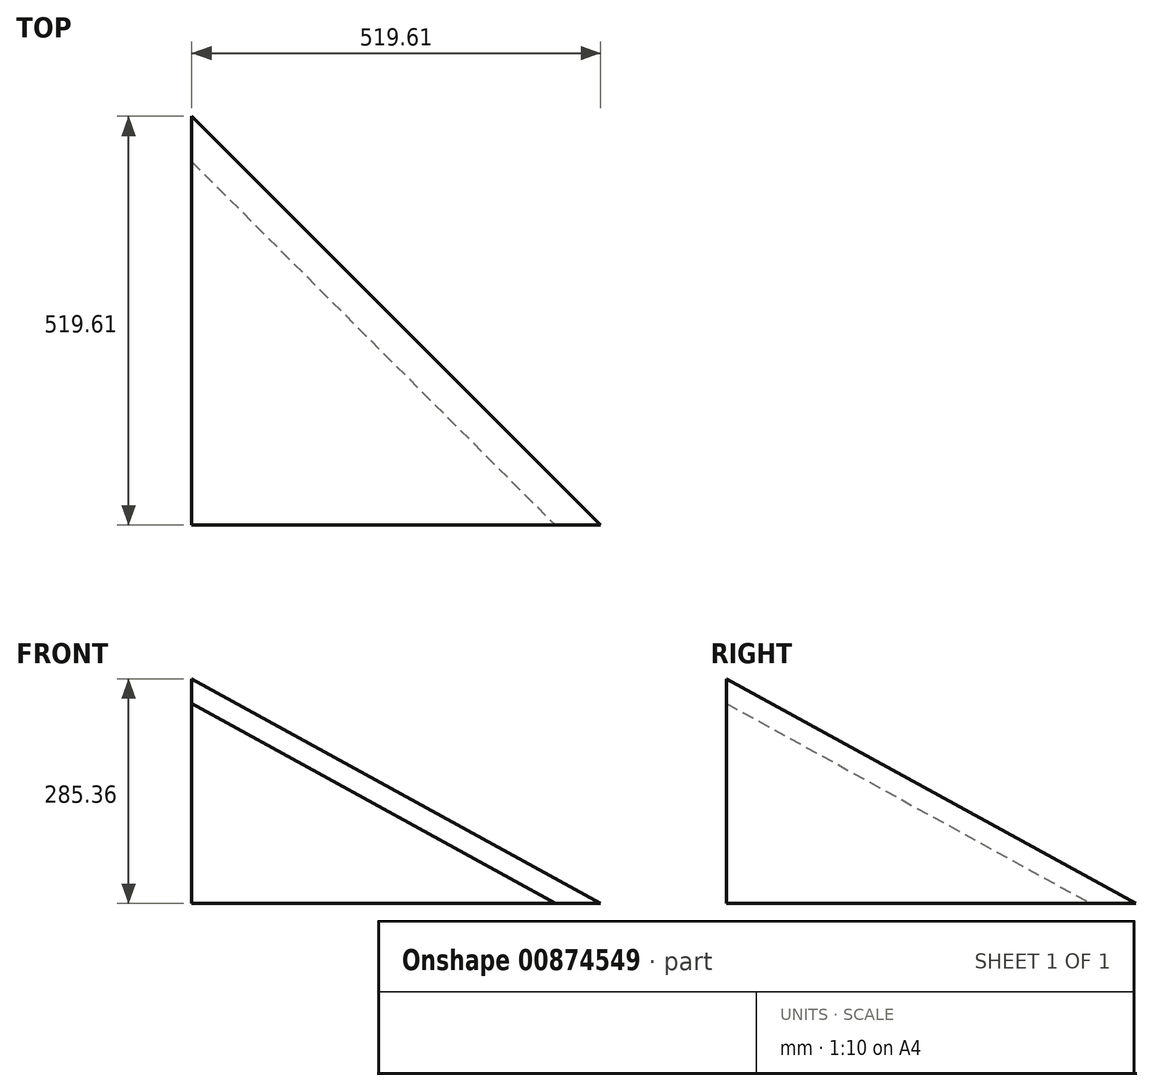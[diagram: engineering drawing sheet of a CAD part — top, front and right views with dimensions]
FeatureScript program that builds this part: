
annotation { "Feature Type Name" : "Feature", "Feature Type Description" : "" }
export const myFeature = defineFeature(function(context is Context, id is Id, definition is map)
    precondition{}
    {
        {
            var Q0;
            Q0=qCreatedBy(makeId("Top.planeOp"),FACE);
            var sketch = newSketch(context, id + "F0", { "sketchPlane" : qUnion([Q0])});
            skLineSegment(sketch, "E0.bottom", {"start": v(0, 0) * mm, "end": v(519.61, 0) * mm});
            skLineSegment(sketch, "E0.left", {"start": v(0, 0) * mm, "end": v(0, 519.61) * mm});
            skLineSegment(sketch, "E1", {"start": v(0, 519.61) * mm, "end": v(519.61, 0) * mm});
            skSolve(sketch);
        }
        {
            var Q0;
            Q0=qCreatedBy(makeId("Front.planeOp"),FACE);
            var sketch = newSketch(context, id + "F1", { "sketchPlane" : qUnion([Q0])});
            skLineSegment(sketch, "E2", {"start": v(0, 0) * mm, "end": v(0, 285.36) * mm});
            skLineSegment(sketch, "E3", {"start": v(519.61, 0) * mm, "end": v(0, 0) * mm});
            skLineSegment(sketch, "E4", {"start": v(0, 285.36) * mm, "end": v(519.61, 0) * mm});
            skSolve(sketch);
        }
        {
            var Q0;
            Q0=qCreatedBy(makeId("Right.planeOp"),FACE);
            var sketch = newSketch(context, id + "F2", { "sketchPlane" : qUnion([Q0])});
            skLineSegment(sketch, "E5", {"start": v(519.61, 0) * mm, "end": v(0, 0) * mm});
            skLineSegment(sketch, "E6", {"start": v(0, 285.36) * mm, "end": v(0, 0) * mm});
            skLineSegment(sketch, "E7", {"start": v(0, 285.36) * mm, "end": v(519.61, 0) * mm});
            skSolve(sketch);
        }
        {
            var Q0;
            Q0=sQuery(id+"F1.wireOp",VERTEX,"E2.end");
            var Q1;
            Q1=sQuery(id+"F0.wireOp",VERTEX,"E0.left.end");
            var Q2;
            Q2=sQuery(id+"F0.wireOp",VERTEX,"E0.bottom.end");
            cPlane(context, id + "F3", {"entities" : qUnion([Q0, Q1, Q2]), "cplaneType" : CPlaneType.THREE_POINT, "offset" : 25 * mm, "width" : 150 * mm, "height" : 150 * mm});
        }
        {
            var Q0;
            Q0=qCreatedBy(id+"F3.planeOp",FACE);
            var sketch = newSketch(context, id + "F4", { "sketchPlane" : qUnion([Q0])});
            skLineSegment(sketch, "E8.0", {"start": v(-108.48, -137.36) * mm, "end": v(-108.48, 455.45) * mm});
            skLineSegment(sketch, "E9.0", {"start": v(-108.48, -137.36) * mm, "end": v(468.2, 0) * mm});
            skLineSegment(sketch, "E10.0", {"start": v(-108.48, 455.45) * mm, "end": v(468.2, 0) * mm});
            skSolve(sketch);
        }
        {
            var Q0;
            Q0 = qSketchRegion(id + "F4", true);
            extrude(context, id + "F5", {"entities" : qUnion([Q0]), "depth" : -25 * mm, "offsetDistance" : 25 * mm});
        }
        {
            var Q0;
            Q0=qCreatedBy(makeId("Top.planeOp"),FACE);
            var sketch = newSketch(context, id + "F6", { "sketchPlane" : qUnion([Q0])});
            skLineSegment(sketch, "E11.0", {"start": v(-45, 577.94) * mm, "end": v(-45, -45) * mm});
            skLineSegment(sketch, "E12.0", {"start": v(-45, -45) * mm, "end": v(592.93, -45) * mm});
            skLineSegment(sketch, "E13", {"start": v(-45, 577.94) * mm, "end": v(0, 577.94) * mm});
            skLineSegment(sketch, "E14", {"start": v(0, 577.94) * mm, "end": v(0, 0) * mm});
            skLineSegment(sketch, "E15", {"start": v(0, 0) * mm, "end": v(592.93, 0) * mm});
            skLineSegment(sketch, "E16", {"start": v(592.93, 0) * mm, "end": v(592.93, -45) * mm});
            skSolve(sketch);
        }
        {
            var Q0;
            Q0=makeQuery(id+"F6.imprint","IMPRINT",FACE,{"disambiguationData":[TD([[makeQuery(id+"F6.imprint","IMPRINT",EDGE,{"derivedFrom":sQuery(id+"F6.wireOp",EDGE,"E11.0")}),1.0]])]});
            extrude(context, id + "F7", {"entities" : qUnion([Q0]), "operationType" : NewBodyOperationType.REMOVE, "depth" : 343 * mm, "offsetDistance" : 25 * mm, "hasSecondDirection" : true, "secondDirectionOppositeDirection" : true, "secondDirectionDepth" : 50 * mm});
        }
        {
            var Q0;
            Q0=qCreatedBy(makeId("Front.planeOp"),FACE);
            var sketch = newSketch(context, id + "F8", { "sketchPlane" : qUnion([Q0])});
            skLineSegment(sketch, "E17.bottom", {"start": v(519.67, 0) * mm, "end": v(0, 0) * mm});
            skLineSegment(sketch, "E17.top", {"start": v(519.67, -31.41) * mm, "end": v(0, -31.41) * mm});
            skLineSegment(sketch, "E17.left", {"start": v(519.67, 0) * mm, "end": v(519.67, -31.41) * mm});
            skLineSegment(sketch, "E17.right", {"start": v(0, 0) * mm, "end": v(0, -31.41) * mm});
            skSolve(sketch);
        }
        {
            var Q0;
            Q0 = qSketchRegion(id + "F8", true);
            extrude(context, id + "F9", {"entities" : qUnion([Q0]), "operationType" : NewBodyOperationType.REMOVE, "oppositeDirection" : true, "depth" : 544 * mm, "offsetDistance" : 25 * mm});
        }
    });
